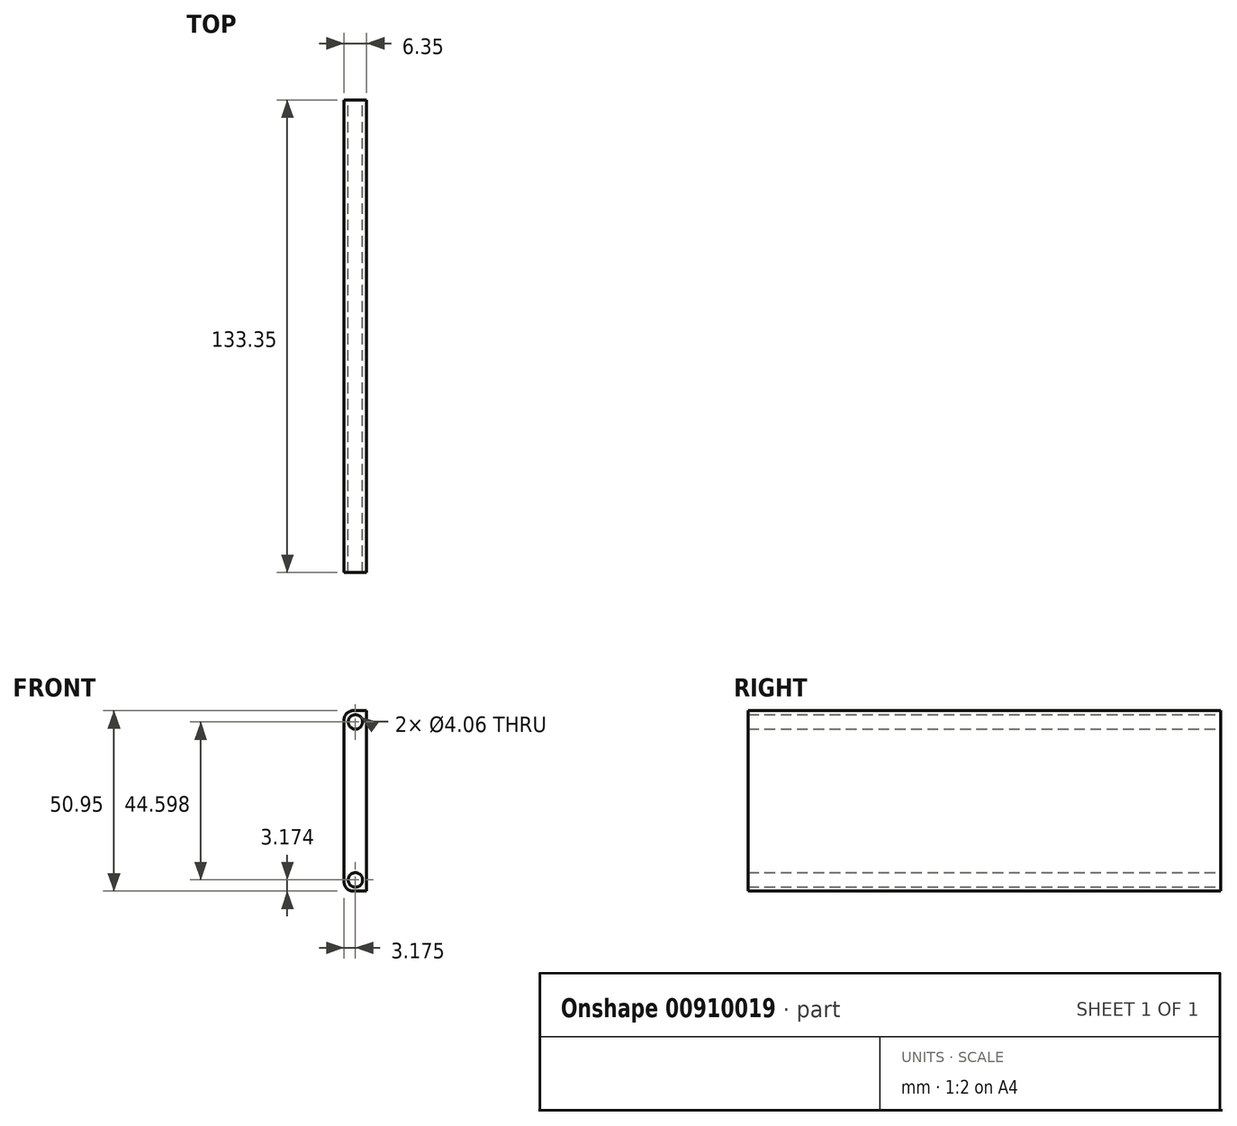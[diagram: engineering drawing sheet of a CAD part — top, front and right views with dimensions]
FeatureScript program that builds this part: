
annotation { "Feature Type Name" : "Feature", "Feature Type Description" : "" }
export const myFeature = defineFeature(function(context is Context, id is Id, definition is map)
    precondition{}
    {
        {
            var Q0;
            Q0=qCreatedBy(makeId("Front.planeOp"),FACE);
            var sketch = newSketch(context, id + "F0", { "sketchPlane" : qUnion([Q0])});
            skLineSegment(sketch, "E0.bottom", {"start": v(2.54, -21.3) * mm, "end": v(6.35, -21.3) * mm});
            skLineSegment(sketch, "E0.top", {"start": v(2.54, 29.66) * mm, "end": v(6.35, 29.66) * mm});
            skLineSegment(sketch, "E0.left", {"start": v(0, -18.75) * mm, "end": v(0, 27.12) * mm});
            skLineSegment(sketch, "E0.right", {"start": v(6.35, -21.3) * mm, "end": v(6.35, 29.66) * mm});
            skPoint(sketch, "E1.visualSharp", {"position": v(0, 29.66) * mm});
            skArc(sketch, "E1.filletArc", {"start": v(2.54, 29.66) * mm, "mid": v(0.74, 28.91) * mm, "end": v(0, 27.12) * mm});
            skPoint(sketch, "E2.visualSharp", {"position": v(0, -21.3) * mm});
            skArc(sketch, "E2.filletArc", {"start": v(0, -18.75) * mm, "mid": v(0.74, -20.55) * mm, "end": v(2.54, -21.3) * mm});
            skCircle(sketch, "E3", {"center": v(3.17, 26.48) * mm, "radius": 2.03 * mm});
            skCircle(sketch, "E4", {"center": v(3.18, -18.12) * mm, "radius": 2.03 * mm});
            skSolve(sketch);
        }
        {
            var Q0;
            Q0=qSketchRegion(id+"F0",true);
            extrude(context, id + "F1", {"entities" : qUnion([Q0]), "depth" : 133.35 * mm, "offsetDistance" : 25.4 * mm});
        }
    });
